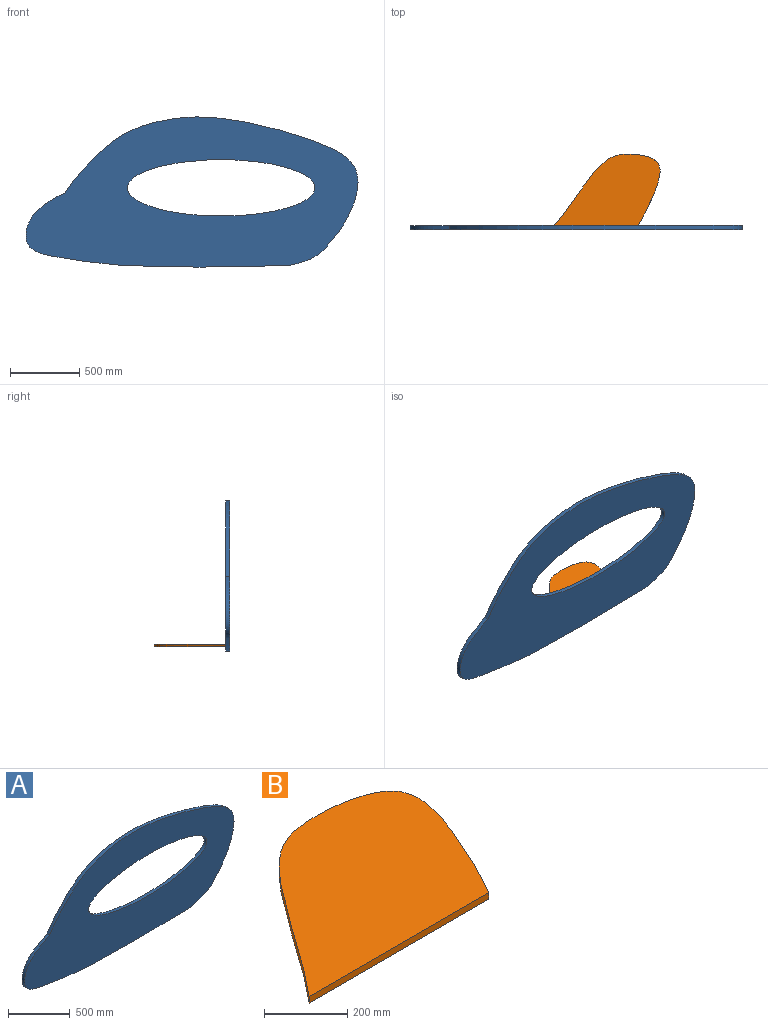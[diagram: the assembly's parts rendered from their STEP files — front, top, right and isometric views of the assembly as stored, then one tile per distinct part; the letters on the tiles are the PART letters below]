
ASSEMBLY  parts=2 mates=1
PART A: 5 faces, bbox 2454.8x30.5x1120.1 mm
  f0: extruded ~1902.6x538.56mm, area 74093.8mm2, adj f1,f2,f3
  f1: extruded ~2118.55x1076.11mm, area 101762.9mm2, adj f0,f2,f3
  f2: plane 2454.77x1120.12mm, normal (0,-1,0), area 1576146.2mm2, adj f0,f1,f4
  f3: plane 2454.77x1120.12mm, normal (0,1,0), area 1576146.2mm2, adj f0,f1,f4
  f4: extruded ~1357.89x409.68mm, area 90874.8mm2, adj f2,f3
PART B: 4 faces, bbox 776.1x527.7x19.1 mm
  f0: extruded ~767.4x518mm, area 28510.7mm2, adj f1,f2,f3
  f1: plane 609.6x19.05mm, normal (0,-1,0), area 11612.9mm2, adj f0,f2,f3
  f2: plane 776.09x527.7mm, normal (0,0,1), area 263612.5mm2, adj f0,f1
  f3: plane 776.09x527.7mm, normal (0,0,-1), area 263612.5mm2, adj f0,f1
PLACE A t=(-31.98,-354.75,-152.03)mm
PLACE B t=(-1532.31,-392.48,156.77)mm
MATE planar A.f3 <-> B.f1  axis (0,1,0) through (-1404.3,-354.75,598.43)mm
